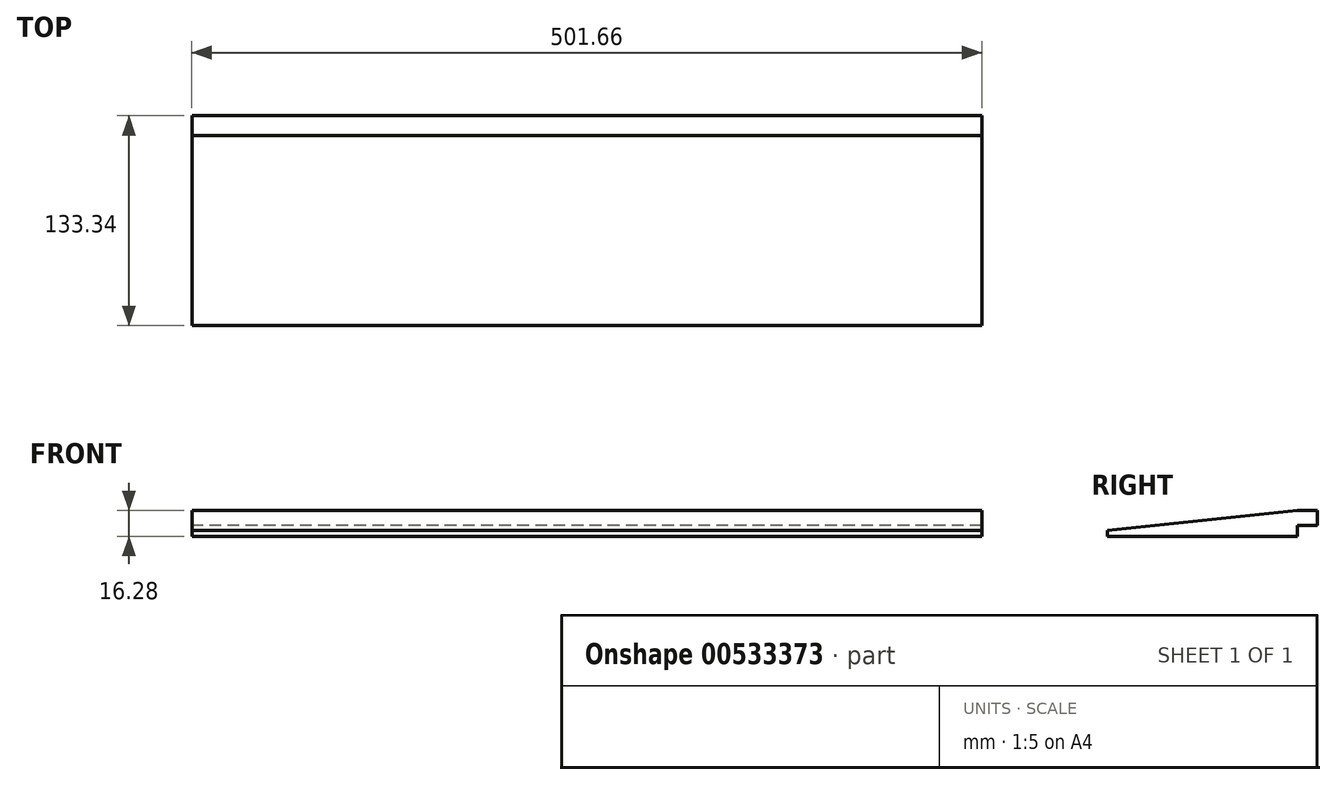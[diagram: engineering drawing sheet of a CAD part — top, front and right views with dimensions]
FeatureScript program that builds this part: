
annotation { "Feature Type Name" : "Feature", "Feature Type Description" : "" }
export const myFeature = defineFeature(function(context is Context, id is Id, definition is map)
    precondition{}
    {
        {
            var Q0;
            Q0=qCreatedBy(makeId("Right.planeOp"),FACE);
            var sketch = newSketch(context, id + "F0", { "sketchPlane" : qUnion([Q0])});
            skLineSegment(sketch, "E0", {"start": v(-66.68, 0) * mm, "end": v(53.98, 0) * mm});
            skLineSegment(sketch, "E1", {"start": v(53.98, 0) * mm, "end": v(53.98, 6.76) * mm});
            skLineSegment(sketch, "E2", {"start": v(53.98, 6.76) * mm, "end": v(66.68, 6.76) * mm});
            skLineSegment(sketch, "E3", {"start": v(66.68, 6.76) * mm, "end": v(66.68, 16.28) * mm});
            skLineSegment(sketch, "E4", {"start": v(66.68, 16.28) * mm, "end": v(53.98, 16.28) * mm});
            skLineSegment(sketch, "E5", {"start": v(53.98, 16.28) * mm, "end": v(-66.68, 3.58) * mm});
            skLineSegment(sketch, "E6", {"start": v(-66.68, 3.58) * mm, "end": v(-66.68, 0) * mm});
            skSolve(sketch);
        }
        {
            var Q0;
            Q0 = qSketchRegion(id + "F0", true);
            extrude(context, id + "F1", {"entities" : qUnion([Q0]), "endBound" : BoundingType.SYMMETRIC, "depth" : 501.65 * mm, "offsetDistance" : 25.4 * mm});
        }
    });
